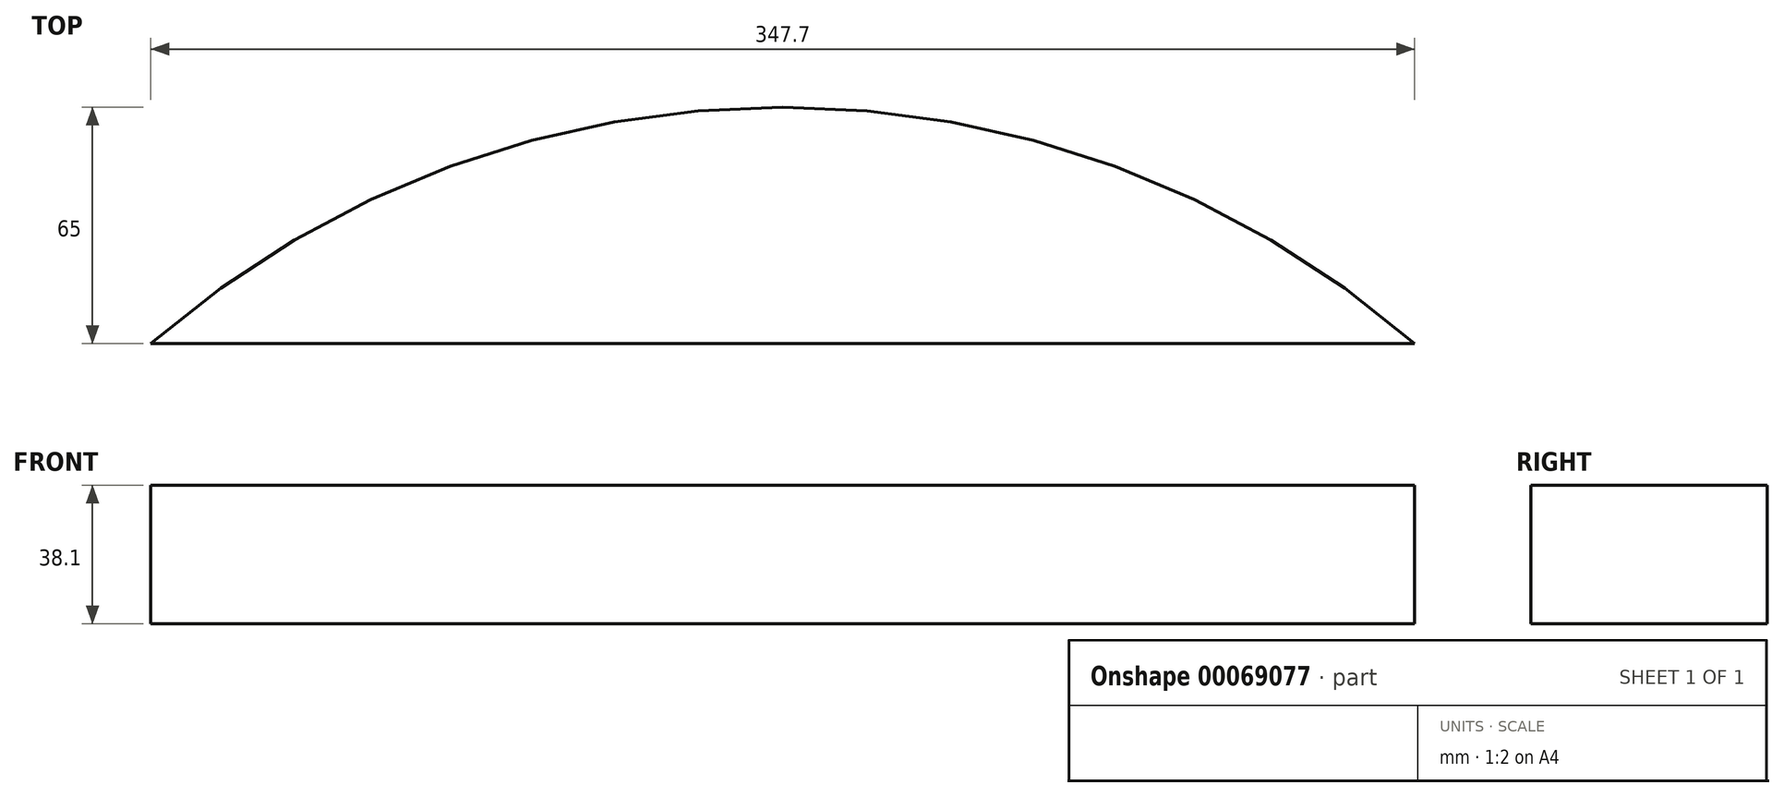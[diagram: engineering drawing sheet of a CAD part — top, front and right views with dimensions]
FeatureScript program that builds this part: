
annotation { "Feature Type Name" : "Feature", "Feature Type Description" : "" }
export const myFeature = defineFeature(function(context is Context, id is Id, definition is map)
    precondition{}
    {
        {
            var Q0;
            Q0=qCreatedBy(makeId("Top.planeOp"),FACE);
            cPlane(context, id + "F0", {"entities" : qUnion([Q0]), "cplaneType" : CPlaneType.OFFSET, "offset" : 1050 * mm, "oppositeDirection" : true, "width" : 152.4 * mm, "height" : 152.4 * mm});
        }
        {
            var Q0;
            Q0=qCreatedBy(makeId("Top.planeOp"),FACE);
            var sketch = newSketch(context, id + "F1", { "sketchPlane" : qUnion([Q0])});
            skCircle(sketch, "E0", {"center": v(0, 0) * mm, "radius": 265 * mm});
            skLineSegment(sketch, "E1.rect.bottom", {"start": v(-200, 200) * mm, "end": v(200, 200) * mm});
            skLineSegment(sketch, "E1.rect.top", {"start": v(-200, -200) * mm, "end": v(200, -200) * mm});
            skLineSegment(sketch, "E1.rect.left", {"start": v(-200, 200) * mm, "end": v(-200, -200) * mm});
            skLineSegment(sketch, "E1.rect.right", {"start": v(200, 200) * mm, "end": v(200, -200) * mm});
            skCircle(sketch, "E2", {"center": v(0, 0) * mm, "radius": 315 * mm, "construction": true});
            skSolve(sketch);
        }
        {
            var Q0;
            {var subQ1=sQuery(id+"F1.wireOp",EDGE,"E0");var subQ8=sQuery(id+"F1.wireOp",EDGE,"E1.rect.bottom");var subQ11=makeQuery(id+"F1.imprint","INTERSECT",VERTEX,{"disambiguationData":[OD(0.0)],"derivedFrom":[subQ1,subQ8]});Q0=makeQuery(id+"F1.imprint","IMPRINT",FACE,{"disambiguationData":[TD([[makeQuery(id+"F1.imprint","IMPRINT",EDGE,{"disambiguationData":[TD([[subQ11,1.0]])],"derivedFrom":subQ1}),1.0]])]});}
            extrude(context, id + "F2", {"entities" : qUnion([Q0]), "oppositeDirection" : true, "depth" : 38.1 * mm});
        }
        {
            var Q0;
            Q0=qCreatedBy(makeId("Front.planeOp"),FACE);
            var sketch = newSketch(context, id + "F3", { "sketchPlane" : qUnion([Q0])});
            skLineSegment(sketch, "E3", {"start": v(0, 0) * mm, "end": v(0, 642.56) * mm, "construction": true});
            skLineSegment(sketch, "E4", {"start": v(100, 80) * mm, "end": v(730, 80) * mm, "construction": true});
            skLineSegment(sketch, "E5", {"start": v(100, 640) * mm, "end": v(730, 640) * mm, "construction": true});
            skLineSegment(sketch, "E6", {"start": v(100, 640) * mm, "end": v(100, 80) * mm, "construction": true});
            skLineSegment(sketch, "E7", {"start": v(730, 640) * mm, "end": v(730, 80) * mm, "construction": true});
            skLineSegment(sketch, "E8", {"start": v(330, 640) * mm, "end": v(330, 80) * mm, "construction": true});
            skLineSegment(sketch, "E9", {"start": v(730, 360) * mm, "end": v(330, 360) * mm, "construction": true});
            skSolve(sketch);
        }
        {
            var Q0;
            Q0=sQuery(id+"F3.wireOp",EDGE,"E9");
            var Q1;
            Q1=sQuery(id+"F3.wireOp",VERTEX,"E9.start");
            cPlane(context, id + "F4", {"entities" : qUnion([Q0, Q1]), "cplaneType" : CPlaneType.CURVE_POINT, "offset" : 152.4 * mm, "width" : 152.4 * mm, "height" : 152.4 * mm});
        }
    });
